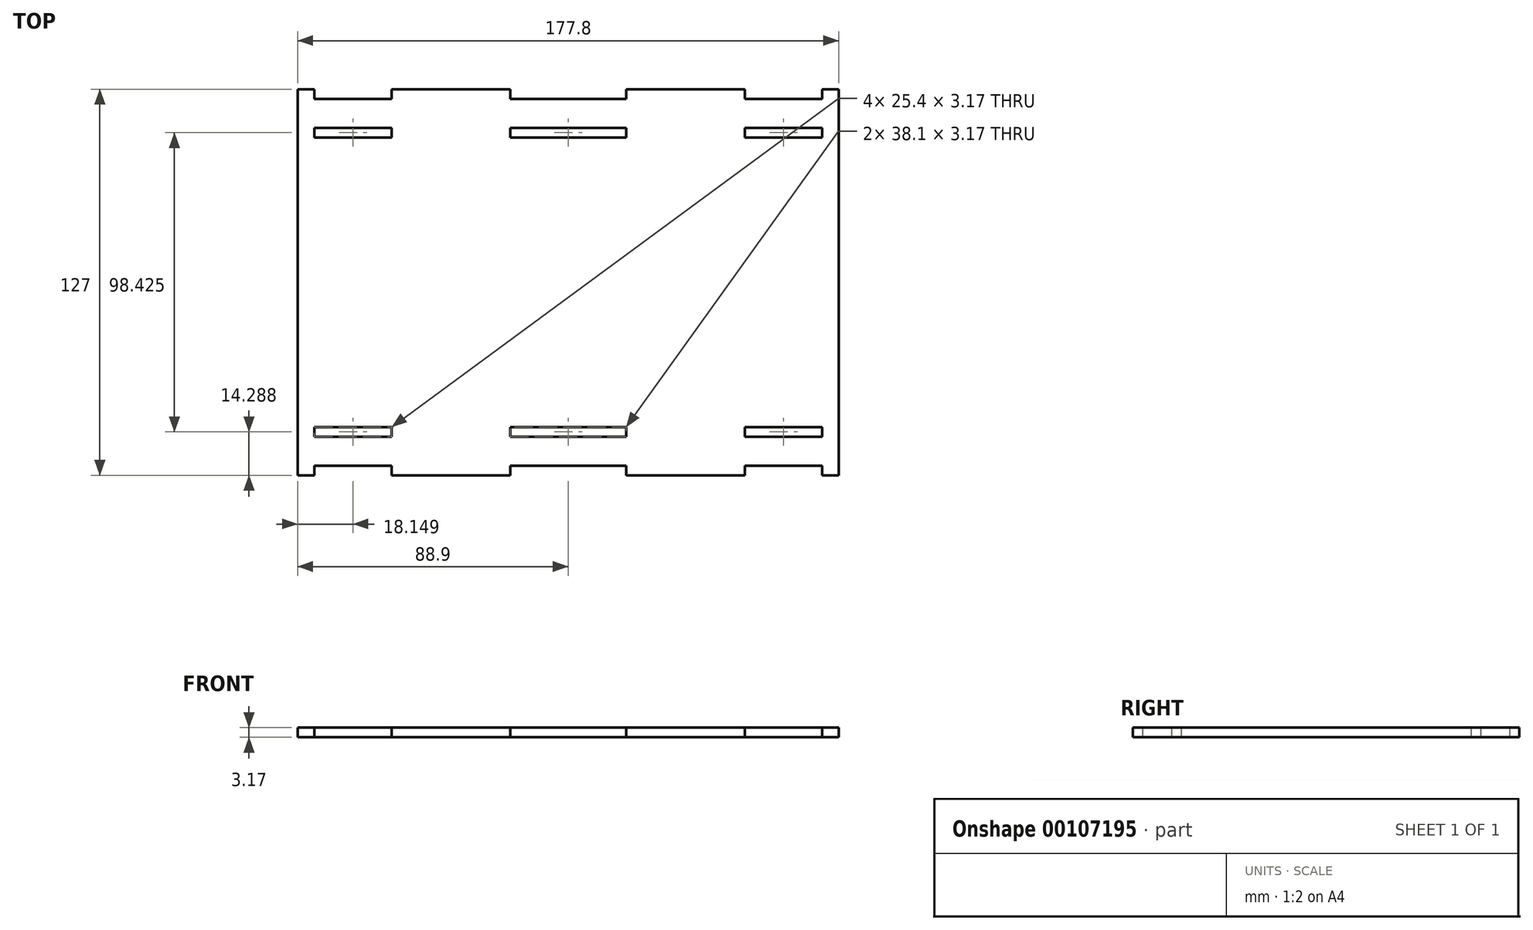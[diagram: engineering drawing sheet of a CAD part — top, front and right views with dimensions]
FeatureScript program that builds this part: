
annotation { "Feature Type Name" : "Feature", "Feature Type Description" : "" }
export const myFeature = defineFeature(function(context is Context, id is Id, definition is map)
    precondition{}
    {
        {
            var Q0;
            Q0=qCreatedBy(makeId("Top.planeOp"),FACE);
            var sketch = newSketch(context, id + "F0", { "sketchPlane" : qUnion([Q0])});
            skLineSegment(sketch, "E0", {"start": v(-76.2, 63.5) * mm, "end": v(-76.2, -63.5) * mm});
            skLineSegment(sketch, "E1.bottom", {"start": v(-76.2, 63.5) * mm, "end": v(-70.75, 63.5) * mm});
            skLineSegment(sketch, "E1.right", {"start": v(101.6, 63.5) * mm, "end": v(101.6, -63.5) * mm});
            skPoint(sketch, "E2", {"position": v(12.7, 76.2) * mm});
            skPoint(sketch, "E3", {"position": v(12.7, 63.5) * mm});
            skLineSegment(sketch, "E4.MirrorCS", {"start": v(70.75, 63.5) * mm, "end": v(70.75, 60.32) * mm});
            skLineSegment(sketch, "E5.MirrorCS", {"start": v(31.75, 60.32) * mm, "end": v(-6.35, 60.32) * mm});
            skLineSegment(sketch, "E6.MirrorCS", {"start": v(-70.75, 60.32) * mm, "end": v(-45.35, 60.32) * mm});
            skLineSegment(sketch, "E7.MirrorCS", {"start": v(-6.35, 63.5) * mm, "end": v(-6.35, 60.32) * mm});
            skLineSegment(sketch, "E8.MirrorCS", {"start": v(-70.75, 63.5) * mm, "end": v(-70.75, 60.32) * mm});
            skLineSegment(sketch, "E9.MirrorCS", {"start": v(96.15, 63.5) * mm, "end": v(96.15, 60.32) * mm});
            skLineSegment(sketch, "E10.MirrorCS", {"start": v(96.15, 60.32) * mm, "end": v(70.75, 60.32) * mm});
            skLineSegment(sketch, "E11.MirrorCS", {"start": v(31.75, 63.5) * mm, "end": v(31.75, 60.32) * mm});
            skLineSegment(sketch, "E12.MirrorCS", {"start": v(-45.35, 63.5) * mm, "end": v(-45.35, 60.32) * mm});
            skLineSegment(sketch, "E13.trimOffspring", {"start": v(-45.35, 63.5) * mm, "end": v(-6.35, 63.5) * mm});
            skLineSegment(sketch, "E14.trimOffspring", {"start": v(31.75, 63.5) * mm, "end": v(70.75, 63.5) * mm});
            skLineSegment(sketch, "E15.trimOffspring", {"start": v(96.15, 63.5) * mm, "end": v(101.6, 63.5) * mm});
            skLineSegment(sketch, "E16.MirrorCS", {"start": v(96.15, 47.62) * mm, "end": v(96.15, 50.8) * mm});
            skLineSegment(sketch, "E17.MirrorCS", {"start": v(70.75, 47.62) * mm, "end": v(70.75, 50.8) * mm});
            skLineSegment(sketch, "E18.MirrorCS", {"start": v(-6.35, 47.62) * mm, "end": v(-6.35, 50.8) * mm});
            skLineSegment(sketch, "E19.MirrorCS", {"start": v(-70.75, 47.62) * mm, "end": v(-70.75, 50.8) * mm});
            skLineSegment(sketch, "E20.MirrorCS", {"start": v(-45.35, 47.62) * mm, "end": v(-45.35, 50.8) * mm});
            skLineSegment(sketch, "E21.MirrorCS", {"start": v(31.75, 47.62) * mm, "end": v(31.75, 50.8) * mm});
            skLineSegment(sketch, "E22.MirrorCS", {"start": v(-70.75, 50.8) * mm, "end": v(-45.35, 50.8) * mm});
            skLineSegment(sketch, "E23.MirrorCS", {"start": v(31.75, 50.8) * mm, "end": v(-6.35, 50.8) * mm});
            skLineSegment(sketch, "E24.MirrorCS", {"start": v(96.15, 47.62) * mm, "end": v(70.75, 47.62) * mm});
            skLineSegment(sketch, "E25.MirrorCS", {"start": v(-45.35, 47.62) * mm, "end": v(-70.75, 47.62) * mm});
            skLineSegment(sketch, "E26.MirrorCS", {"start": v(96.15, 50.8) * mm, "end": v(70.75, 50.8) * mm});
            skLineSegment(sketch, "E27.MirrorCS", {"start": v(31.75, 47.62) * mm, "end": v(-6.35, 47.62) * mm});
            skLineSegment(sketch, "E28.MirrorCS", {"start": v(-70.75, -63.5) * mm, "end": v(-70.75, -60.32) * mm});
            skLineSegment(sketch, "E29.MirrorCS", {"start": v(-76.2, -63.5) * mm, "end": v(-70.75, -63.5) * mm});
            skLineSegment(sketch, "E30.MirrorCS", {"start": v(-6.35, -63.5) * mm, "end": v(-6.35, -60.32) * mm});
            skLineSegment(sketch, "E31.MirrorCS", {"start": v(96.15, -63.5) * mm, "end": v(96.15, -60.32) * mm});
            skLineSegment(sketch, "E32.MirrorCS", {"start": v(31.75, -63.5) * mm, "end": v(31.75, -60.32) * mm});
            skLineSegment(sketch, "E33.MirrorCS", {"start": v(70.75, -63.5) * mm, "end": v(70.75, -60.32) * mm});
            skLineSegment(sketch, "E34.MirrorCS", {"start": v(96.15, -63.5) * mm, "end": v(101.6, -63.5) * mm});
            skLineSegment(sketch, "E35.MirrorCS", {"start": v(-45.35, -63.5) * mm, "end": v(-45.35, -60.32) * mm});
            skPoint(sketch, "E36.MirrorP", {"position": v(12.7, -76.2) * mm});
            skLineSegment(sketch, "E37.MirrorCS", {"start": v(31.75, -63.5) * mm, "end": v(70.75, -63.5) * mm});
            skPoint(sketch, "E38.MirrorP", {"position": v(12.7, -63.5) * mm});
            skLineSegment(sketch, "E39.MirrorCS", {"start": v(-45.35, -63.5) * mm, "end": v(-6.35, -63.5) * mm});
            skLineSegment(sketch, "E40.MirrorCS", {"start": v(-70.75, -60.32) * mm, "end": v(-45.35, -60.32) * mm});
            skLineSegment(sketch, "E41.MirrorCS", {"start": v(96.15, -60.32) * mm, "end": v(70.75, -60.32) * mm});
            skLineSegment(sketch, "E42.MirrorCS", {"start": v(31.75, -60.32) * mm, "end": v(-6.35, -60.32) * mm});
            skLineSegment(sketch, "E43.MirrorCS", {"start": v(31.75, -47.62) * mm, "end": v(31.75, -50.8) * mm});
            skLineSegment(sketch, "E44.MirrorCS", {"start": v(-6.35, -47.62) * mm, "end": v(-6.35, -50.8) * mm});
            skLineSegment(sketch, "E45.MirrorCS", {"start": v(70.75, -47.62) * mm, "end": v(70.75, -50.8) * mm});
            skLineSegment(sketch, "E46.MirrorCS", {"start": v(-45.35, -47.62) * mm, "end": v(-45.35, -50.8) * mm});
            skLineSegment(sketch, "E47.MirrorCS", {"start": v(-70.75, -47.62) * mm, "end": v(-70.75, -50.8) * mm});
            skLineSegment(sketch, "E48.MirrorCS", {"start": v(-70.75, -50.8) * mm, "end": v(-45.35, -50.8) * mm});
            skLineSegment(sketch, "E49.MirrorCS", {"start": v(31.75, -50.8) * mm, "end": v(-6.35, -50.8) * mm});
            skLineSegment(sketch, "E50.MirrorCS", {"start": v(-45.35, -47.62) * mm, "end": v(-70.75, -47.62) * mm});
            skLineSegment(sketch, "E51.MirrorCS", {"start": v(31.75, -47.62) * mm, "end": v(-6.35, -47.62) * mm});
            skLineSegment(sketch, "E52.MirrorCS", {"start": v(96.15, -50.8) * mm, "end": v(70.75, -50.8) * mm});
            skLineSegment(sketch, "E53.MirrorCS", {"start": v(96.15, -47.62) * mm, "end": v(96.15, -50.8) * mm});
            skLineSegment(sketch, "E54.MirrorCS", {"start": v(96.15, -47.62) * mm, "end": v(70.75, -47.62) * mm});
            skSolve(sketch);
        }
        {
            var Q0;
            Q0=makeQuery(id+"F0.imprint","IMPRINT",FACE,{"disambiguationData":[TD([[makeQuery(id+"F0.imprint","IMPRINT",EDGE,{"derivedFrom":sQuery(id+"F0.wireOp",EDGE,"E1.bottom")}),-1.0]])]});
            extrude(context, id + "F1", {"entities" : qUnion([Q0]), "depth" : 3.17 * mm});
        }
    });
